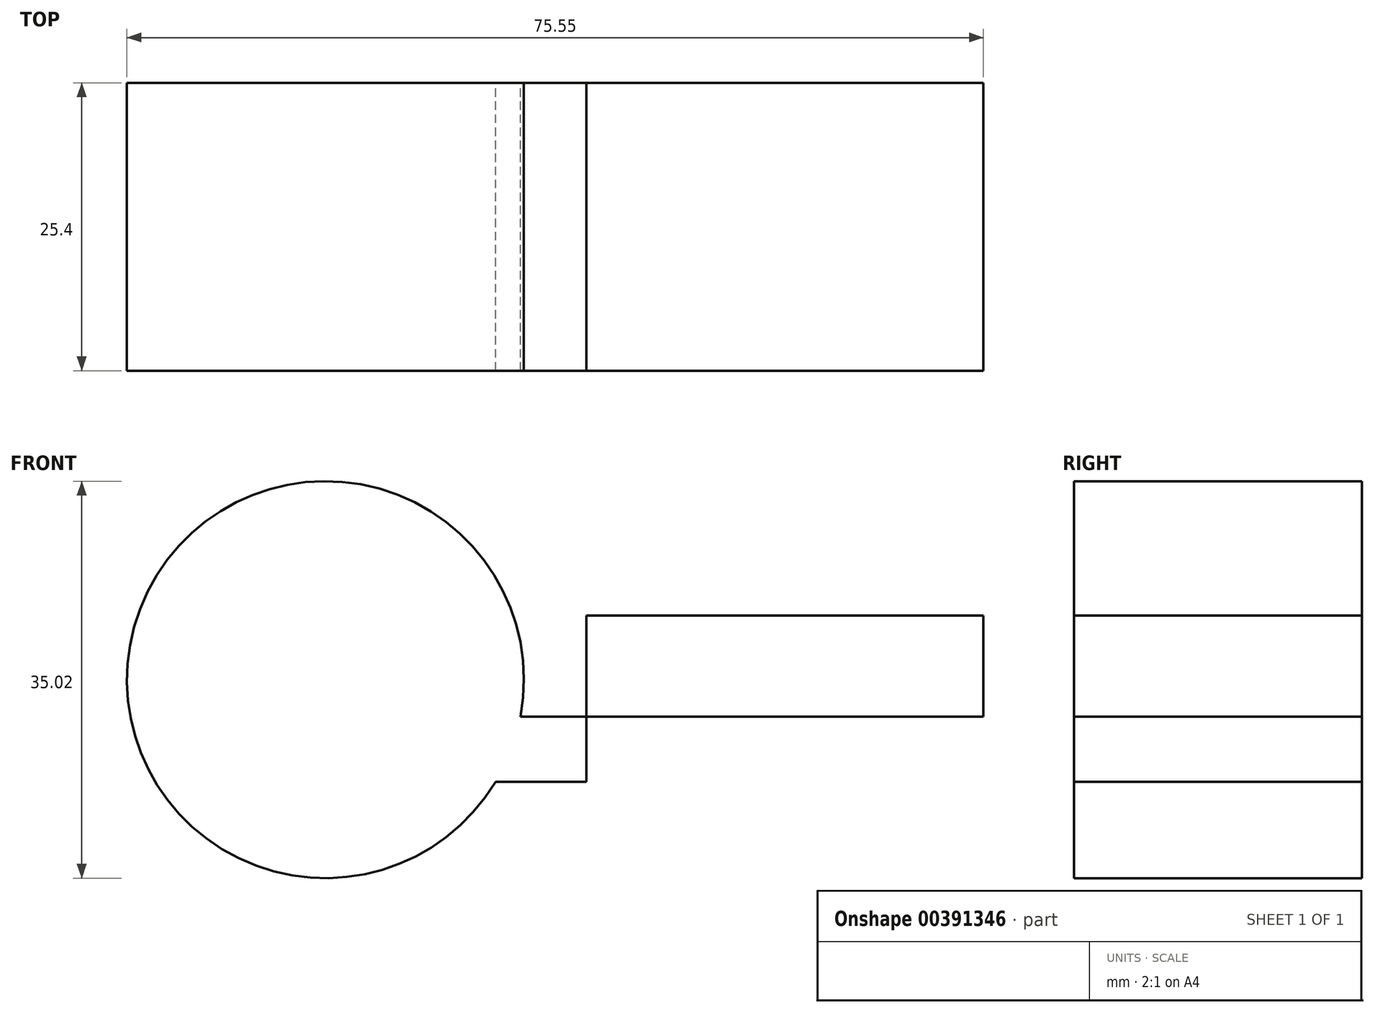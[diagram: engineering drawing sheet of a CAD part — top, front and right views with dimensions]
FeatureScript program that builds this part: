
annotation { "Feature Type Name" : "Feature", "Feature Type Description" : "" }
export const myFeature = defineFeature(function(context is Context, id is Id, definition is map)
    precondition{}
    {
        {
            var Q0;
            Q0=qCreatedBy(makeId("Front.planeOp"),FACE);
            var sketch = newSketch(context, id + "F0", { "sketchPlane" : qUnion([Q0])});
            skCircle(sketch, "E0", {"center": v(-15.01, 9.01) * mm, "radius": 17.5 * mm});
            skLineSegment(sketch, "E1.bottom", {"start": v(8, 14.65) * mm, "end": v(43.03, 14.65) * mm});
            skLineSegment(sketch, "E1.top", {"start": v(8, 5.75) * mm, "end": v(43.03, 5.75) * mm});
            skLineSegment(sketch, "E1.left", {"start": v(8, 14.65) * mm, "end": v(8, 5.75) * mm});
            skLineSegment(sketch, "E1.right", {"start": v(43.03, 14.65) * mm, "end": v(43.03, 5.75) * mm});
            skLineSegment(sketch, "E2.bottom", {"start": v(8, 5.75) * mm, "end": v(-3, 5.75) * mm});
            skLineSegment(sketch, "E2.top", {"start": v(8, 0) * mm, "end": v(-3, 0) * mm});
            skLineSegment(sketch, "E2.left", {"start": v(8, 5.75) * mm, "end": v(8, 0) * mm});
            skLineSegment(sketch, "E2.right", {"start": v(-3, 5.75) * mm, "end": v(-3, 0) * mm});
            skSolve(sketch);
        }
        {
            var Q0;
            {var subQ5=sQuery(id+"F0.wireOp",EDGE,"E2.right");Q0=makeQuery(id+"F0.imprint","IMPRINT",FACE,{"disambiguationData":[TD([[makeQuery(id+"F0.imprint","IMPRINT",EDGE,{"derivedFrom":subQ5}),-1.0]])]});}
            var Q1;
            {var subQ5=sQuery(id+"F0.wireOp",EDGE,"E2.left");Q1=makeQuery(id+"F0.imprint","IMPRINT",FACE,{"disambiguationData":[TD([[makeQuery(id+"F0.imprint","IMPRINT",EDGE,{"derivedFrom":subQ5}),-1.0]])]});}
            var Q2;
            {var subQ5=sQuery(id+"F0.wireOp",EDGE,"E2.right");Q2=makeQuery(id+"F0.imprint","IMPRINT",FACE,{"disambiguationData":[TD([[makeQuery(id+"F0.imprint","IMPRINT",EDGE,{"derivedFrom":subQ5}),1.0]])]});}
            var Q3;
            Q3=makeQuery(id+"F0.imprint","IMPRINT",FACE,{"disambiguationData":[TD([[makeQuery(id+"F0.imprint","IMPRINT",EDGE,{"derivedFrom":sQuery(id+"F0.wireOp",EDGE,"E1.bottom")}),-1.0]])]});
            extrude(context, id + "F1", {"entities" : qUnion([Q0, Q1, Q2, Q3]), "depth" : 25.4 * mm});
        }
    });
